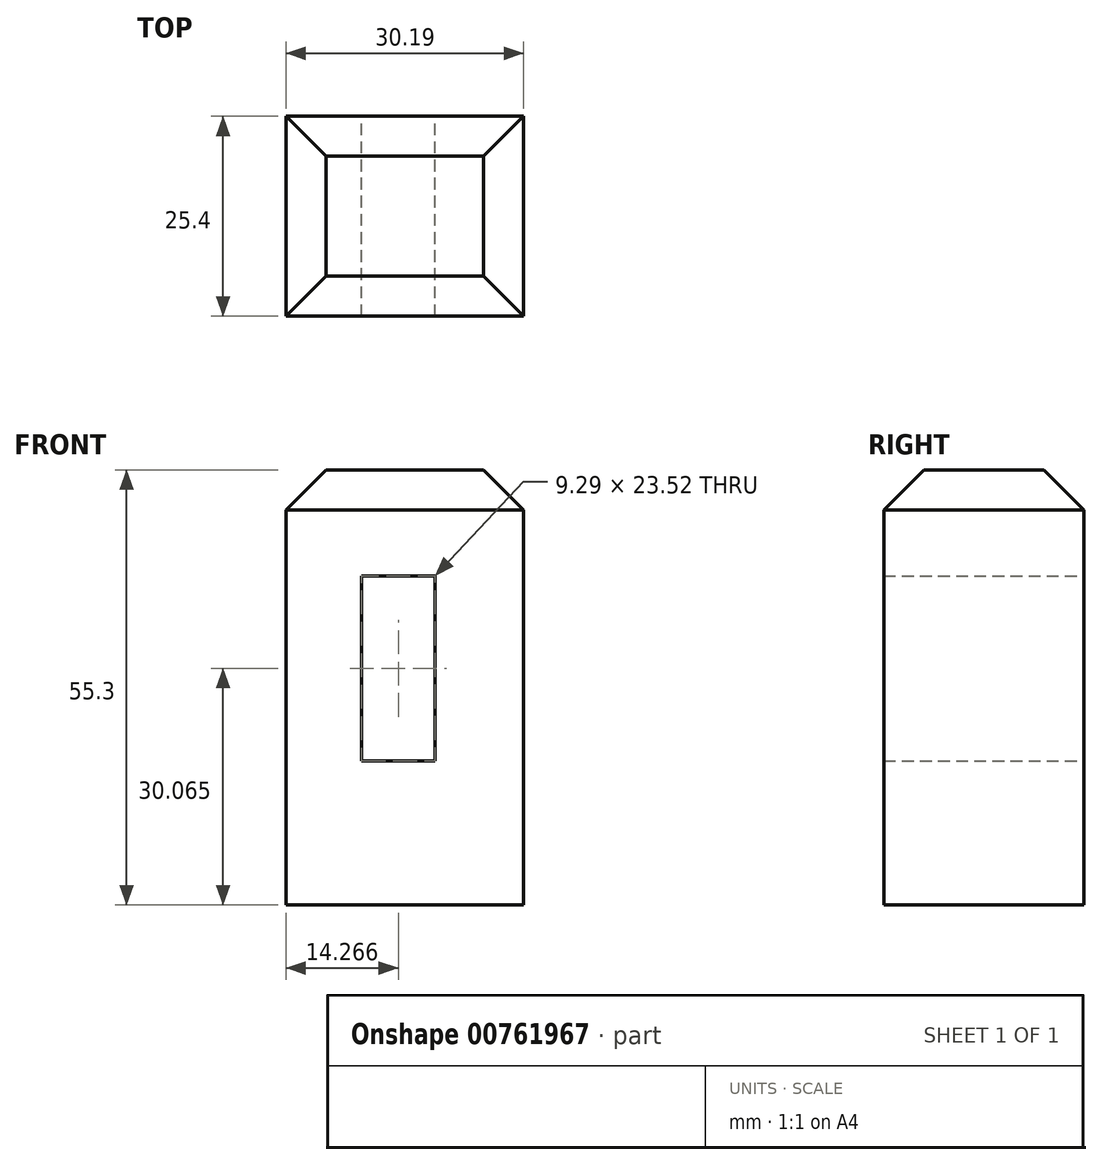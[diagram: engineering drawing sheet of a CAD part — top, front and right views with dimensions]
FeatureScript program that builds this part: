
annotation { "Feature Type Name" : "Feature", "Feature Type Description" : "" }
export const myFeature = defineFeature(function(context is Context, id is Id, definition is map)
    precondition{}
    {
        {
            var Q0;
            Q0=qCreatedBy(makeId("Front.planeOp"),FACE);
            var sketch = newSketch(context, id + "F0", { "sketchPlane" : qUnion([Q0])});
            skLineSegment(sketch, "E0.bottom", {"start": v(-115.92, 60.73) * mm, "end": v(-85.73, 60.73) * mm});
            skLineSegment(sketch, "E0.top", {"start": v(-115.92, 5.43) * mm, "end": v(-85.73, 5.43) * mm});
            skLineSegment(sketch, "E0.left", {"start": v(-115.92, 60.73) * mm, "end": v(-115.92, 5.43) * mm});
            skLineSegment(sketch, "E0.right", {"start": v(-85.73, 60.73) * mm, "end": v(-85.73, 5.43) * mm});
            skLineSegment(sketch, "E1.bottom", {"start": v(-106.3, 47.25) * mm, "end": v(-97.01, 47.25) * mm});
            skLineSegment(sketch, "E1.top", {"start": v(-106.3, 23.73) * mm, "end": v(-97.01, 23.73) * mm});
            skLineSegment(sketch, "E1.left", {"start": v(-106.3, 47.25) * mm, "end": v(-106.3, 23.73) * mm});
            skLineSegment(sketch, "E1.right", {"start": v(-97.01, 47.25) * mm, "end": v(-97.01, 23.73) * mm});
            skSolve(sketch);
        }
        {
            var Q0;
            Q0=makeQuery(id+"F0.imprint","IMPRINT",FACE,{"disambiguationData":[TD([[makeQuery(id+"F0.imprint","IMPRINT",EDGE,{"derivedFrom":sQuery(id+"F0.wireOp",EDGE,"E0.bottom")}),-1.0]])]});
            extrude(context, id + "F1", {"entities" : qUnion([Q0]), "depth" : 25.4 * mm, "offsetDistance" : 25.4 * mm});
        }
        {
            var Q0;
            Q0=makeQuery(id+"F1.opExtrude","CAP_EDGE",EDGE,{"disambiguationData":[OSD([sQuery(id+"F0.wireOp",EDGE,"E0.bottom")])],"isStart":false});
            var Q1;
            Q1=makeQuery(id+"F1.opExtrude","CAP_EDGE",EDGE,{"disambiguationData":[OSD([sQuery(id+"F0.wireOp",EDGE,"E0.bottom")])],"isStart":true});
            var Q2;
            Q2=makeQuery(id+"F1.opExtrude","SWEPT_EDGE",EDGE,{"disambiguationData":[OSD([sQuery(id+"F0.wireOp",EDGE,"E0.bottom"),sQuery(id+"F0.wireOp",EDGE,"E0.right")])]});
            var Q3;
            Q3=makeQuery(id+"F1.opExtrude","SWEPT_EDGE",EDGE,{"disambiguationData":[OSD([sQuery(id+"F0.wireOp",EDGE,"E0.bottom"),sQuery(id+"F0.wireOp",EDGE,"E0.left")])]});
            chamfer(context, id + "F2", {"entities" : qUnion([Q0, Q1, Q2, Q3]), "width" : 5.08 * mm, "tangentPropagation" : true});
        }
    });
